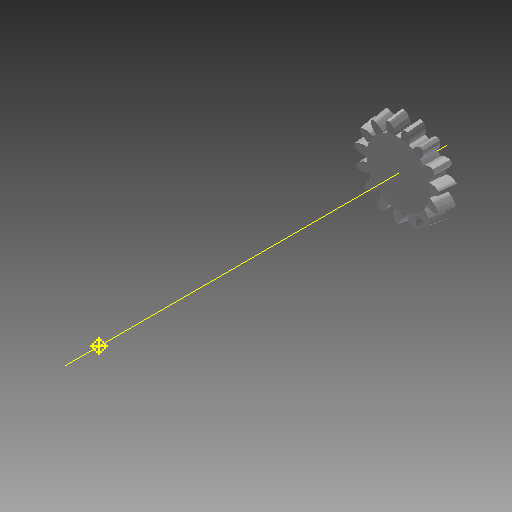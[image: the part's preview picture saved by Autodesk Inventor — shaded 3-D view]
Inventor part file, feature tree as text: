
AUTODESK INVENTOR PART (.ipt)
format: ipt  version: 2017 (Build 210142000, 142)  size: 501,248 bytes
history: native  units: mm
features: other x24, loft x2, pattern_circular x2, sketch x2
ambient origin geometry x6: Origin, XZ Plane, X Axis, Y Axis, Z Axis, Center Point
bodies: Solid1 (feature_tree)
feature tree (30):
  other  "Top Point"
  other  "Mesh Plane2"
  other  "Teeth Body"
  other  "Start Point"
  other  "Tooth Plane"
  other  "Start Sketch"
  other  "End Point"
  other  "3D Sketch Right"
  other  "End Plane Right"
  loft  "Loft Right"
  pattern_circular  "Circular Pattern Right"  [2 undecoded]
  other  "3D Sketch Left"
  other  "End Plane Left"
  loft  "Loft Left"
  pattern_circular  "Circular Pattern Left"  Angle=90.0deg  [1 undecoded]
  other  "Fix Body"
  sketch  "Sketch8"  dims[d2=42.950477mm d3=7.62mm d4=150.824298mm d5=90.0deg d7=7.258789mm d8=8.466511mm d9=15.816659mm d11=7.894621mm d12=6.889845mm d15=8.036182mm d16=15.012743mm d17=0.0mm d18=90.0deg d19=0.0mm d20=90.0deg d21=150.0mm d22=360.0deg d26=314.208686mm d27=7.832641mm d28=38.1mm d29=-1.253891mm d30=6.889845mm d31=8.036182mm d32=15.012743mm d35=0.0mm d37=0.0mm d39=0.0mm d40=90.0deg d41=150.0mm d42=360.0deg d46=90.0deg d47=90.0deg d48=0.0mm d49=0.0mm d50=90.0deg d51=2.094395mm d52=0.0mm d53=0.0mm d54=0.0mm d56=20.24081mm d57=23.292902mm d58=15.493652mm d59=22.10899mm d60=14.706153mm d61=22.10899mm d62=14.706153mm d63=90.0deg d64=90.0deg d65=314.208686mm d66=31.5mm d67=38.1mm d68=-1.253891mm d69=7.832641mm d70=8.036182mm d71=15.012743mm d72=6.889845mm d73=14.706153mm d74=22.10899mm d75=0.0mm d76=90.0deg d77=0.0mm d78=90.0deg d79=0.0mm d80=90.0deg d81=150.0mm d82=360.0deg d84=10.0mm d85=20.0mm d86=20.0mm d87=10.0mm d88=0.0mm d89=0.0mm]
  other  "Mesh Plane"
  other  "Top Plane"
  other  "Teeth Body Sketch"
  other  "End Plane"
  other  "End Sketch"
  other  "Helical Curve Left"
  other  "End Sketch Left"
  other  "Body Sketch"
  sketch  "Sketch6"  dims[d0=38.1mm d1=32.051859mm]
  other  "Srf1"
  other  "Helical Curve Right"
  other  "End Sketch Right"
  other  "Pitch Diameter"
note: 3 required parameter values undecoded (feature->parameter linkage not recoverable at this tier; creation-order binding heuristic only, values carry confidence <= 0.55)
